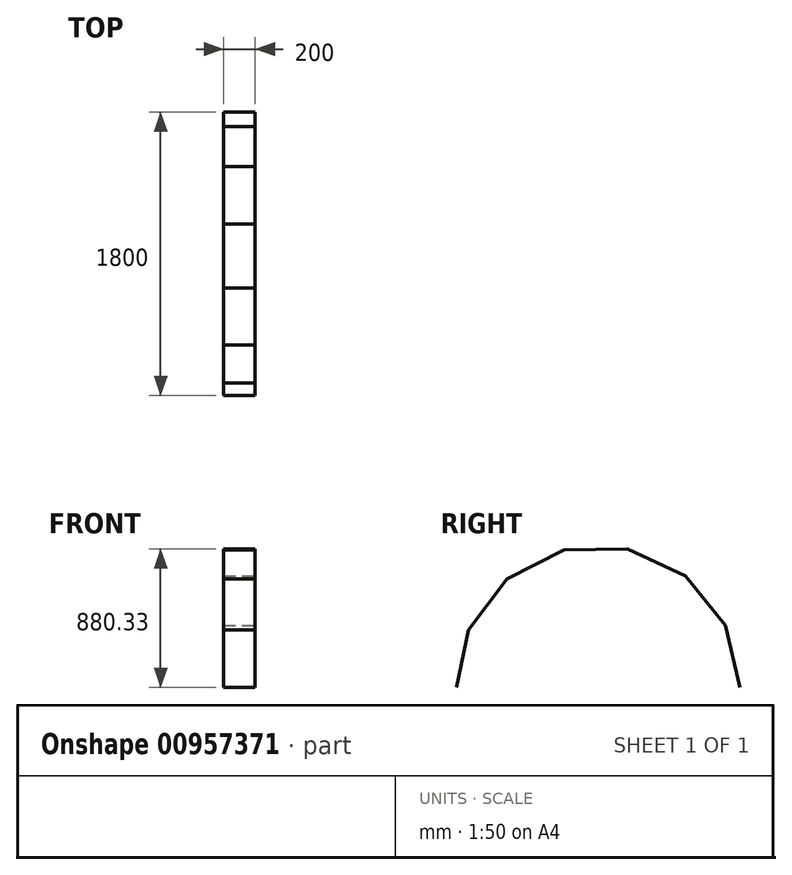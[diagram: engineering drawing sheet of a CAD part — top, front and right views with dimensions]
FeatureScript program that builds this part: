
annotation { "Feature Type Name" : "Feature", "Feature Type Description" : "" }
export const myFeature = defineFeature(function(context is Context, id is Id, definition is map)
    precondition{}
    {
        {
            var Q0;
            Q0=qCreatedBy(makeId("Right.planeOp"),FACE);
            var sketch = newSketch(context, id + "F0", { "sketchPlane" : qUnion([Q0])});
            skLineSegment(sketch, "E0", {"start": v(-900, 0) * mm, "end": v(-822.2, 366.06) * mm});
            skLineSegment(sketch, "E1", {"start": v(-822.2, 366.06) * mm, "end": v(-578.5, 689.44) * mm});
            skLineSegment(sketch, "E2", {"start": v(-578.5, 689.44) * mm, "end": v(-217.73, 873.27) * mm});
            skLineSegment(sketch, "E3", {"start": v(-217.73, 873.27) * mm, "end": v(187.12, 880.33) * mm});
            skLineSegment(sketch, "E4", {"start": v(187.12, 880.33) * mm, "end": v(554.1, 709.2) * mm});
            skLineSegment(sketch, "E5", {"start": v(554.1, 709.2) * mm, "end": v(808.91, 394.53) * mm});
            skLineSegment(sketch, "E6", {"start": v(808.91, 394.53) * mm, "end": v(900, 0) * mm});
            skSolve(sketch);
        }
        {
            var Q0;
            Q0=sQuery(id+"F0.wireOp",EDGE,"E0");
            var Q1;
            Q1=sQuery(id+"F0.wireOp",EDGE,"E4");
            var Q2;
            Q2=sQuery(id+"F0.wireOp",EDGE,"E2");
            var Q3;
            Q3=sQuery(id+"F0.wireOp",EDGE,"E3");
            var Q4;
            Q4=sQuery(id+"F0.wireOp",EDGE,"E6");
            var Q5;
            Q5=sQuery(id+"F0.wireOp",EDGE,"E1");
            var Q6;
            Q6=sQuery(id+"F0.wireOp",EDGE,"E5");
            extrude(context, id + "F1", {"bodyType" : ToolBodyType.SURFACE, "surfaceEntities" : qUnion([Q0, Q1, Q2, Q3, Q4, Q5, Q6]), "depth" : 200 * mm, "offsetDistance" : 25 * mm});
        }
    });
